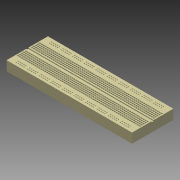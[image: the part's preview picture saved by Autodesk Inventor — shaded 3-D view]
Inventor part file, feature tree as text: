
AUTODESK INVENTOR PART (.ipt)
format: ipt  version: 2014 (Build 180170000, 170)  size: 4,493,824 bytes
history: native  units: in
note: dims shown in document units (in); Inventor stores cm internally (conversion verified against a paired STEP export)
features: sketch x6, extrude x5, pattern_linear x4, chamfer x3, plane x2, mirror x2, emboss x1
ambient origin geometry x8: Origin, YZ Plane, XZ Plane, XY Plane, X Axis, Y Axis, Z Axis, Center Point
bodies: Solid1 (feature_tree)
feature tree (23):
  extrude  "Extrusion1"  Depth=2.14in
  extrude  "Extrusion2"  Depth=0.1in
  sketch  "Sketch3"  dims[d19=0.05in d20=0.0in d21=0.065in]
  extrude  "Extrusion3"  Depth=0.065in
  plane  "Work Plane1"
  chamfer  "Chamfer1"  Distance=0.05in
  pattern_linear  "Rectangular Pattern1"  Count1=64 Spacing1=0.1in
  extrude  "Extrusion4"  Depth=1.9685in
  chamfer  "Chamfer2"  Distance=0.05in
  pattern_linear  "Rectangular Pattern2"  Spacing1=0.01in  [1 undecoded]
  plane  "Work Plane2"
  extrude  "Extrusion5"  Depth=25.1969in
  chamfer  "Chamfer3"  Distance=1.9685in
  pattern_linear  "Rectangular Pattern3"  Spacing1=0.04in  [1 undecoded]
  pattern_linear  "Rectangular Pattern4"  Spacing1=0.135in  [1 undecoded]
  mirror  "Mirror3"
  mirror  "Mirror4"
  emboss  "Emboss1"
  sketch  "Sketch6"  dims[d27=0.01in d28=0.125in d29=45.0deg d30=25.1969in d32=0.1in d33=1.9685in d35=0.1in d36=0.05in d37=0.0in d38=0.01in d39=0.125in d40=45.0deg d41=25.1969in d43=0.1in d44=1.9685in d46=0.1in d47=0.04in d50=0.135in d51=0.075in d52=0.075in d53=0.05in d54=0.0in d55=0.01in d56=0.125in d57=45.0deg d58=1.9685in d60=0.1in d61=0.7874in d63=0.1in d64=1.9685in d66=0.6in d67=0.05in d68=0.0in]
  sketch  "Sketch1"  dims[d10=6.496in d11=2.14in]
  sketch  "Sketch2"  dims[d15=0.5in d16=0.0in d17=0.1in]
  sketch  "Sketch4"  dims[d23=0.0655in]
  sketch  "Sketch5"  dims[d24=0.475in d25=0.05in d26=0.0in]
note: 3 required parameter values undecoded (feature->parameter linkage not recoverable at this tier; creation-order binding heuristic only, values carry confidence <= 0.55)
